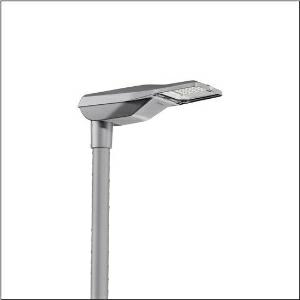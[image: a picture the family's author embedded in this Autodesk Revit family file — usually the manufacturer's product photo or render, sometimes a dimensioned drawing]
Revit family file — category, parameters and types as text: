
# Revit family: streetlight_sl_21_iq_micro___p0_8a_5xe1u31g08db_89ec
name_source: partatom
category: Lighting Fixtures
units: mm (PartAtom-declared; Revit-internal decimal feet)

## family parameters
Cut with Voids When Loaded = No
Host = Face
Light Source = No
Part Type = Normal
Room Calculation Point = No
Round Connector Dimension = Use Diameter
Shared = No

## types (1)
- --- (1 x LED, 4750 lm, 36.4 W, 3000K)
    Apparent Load = 36 VA
    CIE Flux Codes = 33 69 96 100 100
    Color Rendering = 70
    Color Temperature = 3000K
    Default Elevation = 1800 mm
    Description = Streetlight SL 21 iQ micro, mast luminaire, primary light control with lens, of PMMA, primary optical cover: cover, of toughened safety glass, transparent, light distribution: P0.8a, light emission: direct distribution, primary light characteristic: asymmetric, installation type: post-top, side-entry, LED, High Power LED, rated luminous flux: 4.750lm, luminous efficacy: 131lm/W, light colour: 730, colour temperature: 3000K, control gear: iQ Street-Remote, control: pre-setting: linear dimming characteristic, Street-Remote, Auto-Match, Temp-Guard, Lumen-Switch, Night-Set, Smart-Wire, Light-Fading, Desk-Remote (wireless, voltage-free reading and setting of iQ features in the workshop via application-optimized NFC function/RFID function), optimised constant luminous flux control (CLO 2.0), mains connection: 220..240V, AC, 50/60Hz, start of lifetime: 36W, end of service life: 38W, reduction: 16W, luminaire housing, of diecast aluminium, powder-coated, Siteco® metallic grey (DB 702S), corrosivity category C5 mid according to DIN EN ISO 12944, please order mast flange separately, inclination adjustable: 0°, 5°, 10°, 15°, sealing non-destructively replaceable, multi-level sealing system, length: 528mm, width: 235mm, height: 110mm, mast flange for spigot size: 42mm (side-entry): 5XC10008XM4, 60/48mm (side-entry/post-top): 5XC10108XM2, 76/60mm (side-entry/post-top): 5XC10108XM1, protection rating (complete): IP66, insulation class (complete): insulation class II (safety insulation), certification: CE, ENEC, ENEC+, VDE, impact resistance: IK09, permissible operating ambient temperature for outdoor applications: -40..+50°C, standard-compliant lighting for roads and squares, packaging unit: 1 piece

Light Distribution: P0.8a
    Height = 110 mm
    Lamp = 1 x LED
    Lamp Light Flux = 4750 lm
    Lamp Power = 36.4 W
    Lamp count = 1
    Length = 528 mm
    Luminous efficacy = 130 lm/W
    Manufacturer = Siteco
    ModVariant = No
    Model = 5XE1U31G08DB
    Number of Poles = 1
    OnlyDefault = Yes
    Power Factor = 1
    Product Name = Streetlight SL 21 iQ micro | P0.8a
    Product group = mast luminaire | pylon top
    ProductGroupID = 6100
    Protection Class = Protection class II
    Protection Degree = IP 66
    RLX_Detail_Level = 1
    RLX_Emergency_Light_Flux = 0 lm
    RLX_Emergency_Type = 0
    RLX_Emergency_Type_DB = No
    RlxData = <blob elided: 99273 chars, md5=0e2f14f5>
    Socket = socket
    Standby Power = 0 W
    System Light Flux = 4750 lm
    System Power = 36 W
    Type Comments = factory setting: luminous flux: 100 % | dim-lin: 254 | 715 mA
    Type Image = l_1006881.jpg
    URL = http://relux.com
    VarID = @adj_070044
    Voltage = 0 V
    Weight = 0.00 kg
    Width = 235 mm

## geometry (parser evidence)
native form markers: Blend x4, Sweep x10
no freeform markers — native parametric forms only
